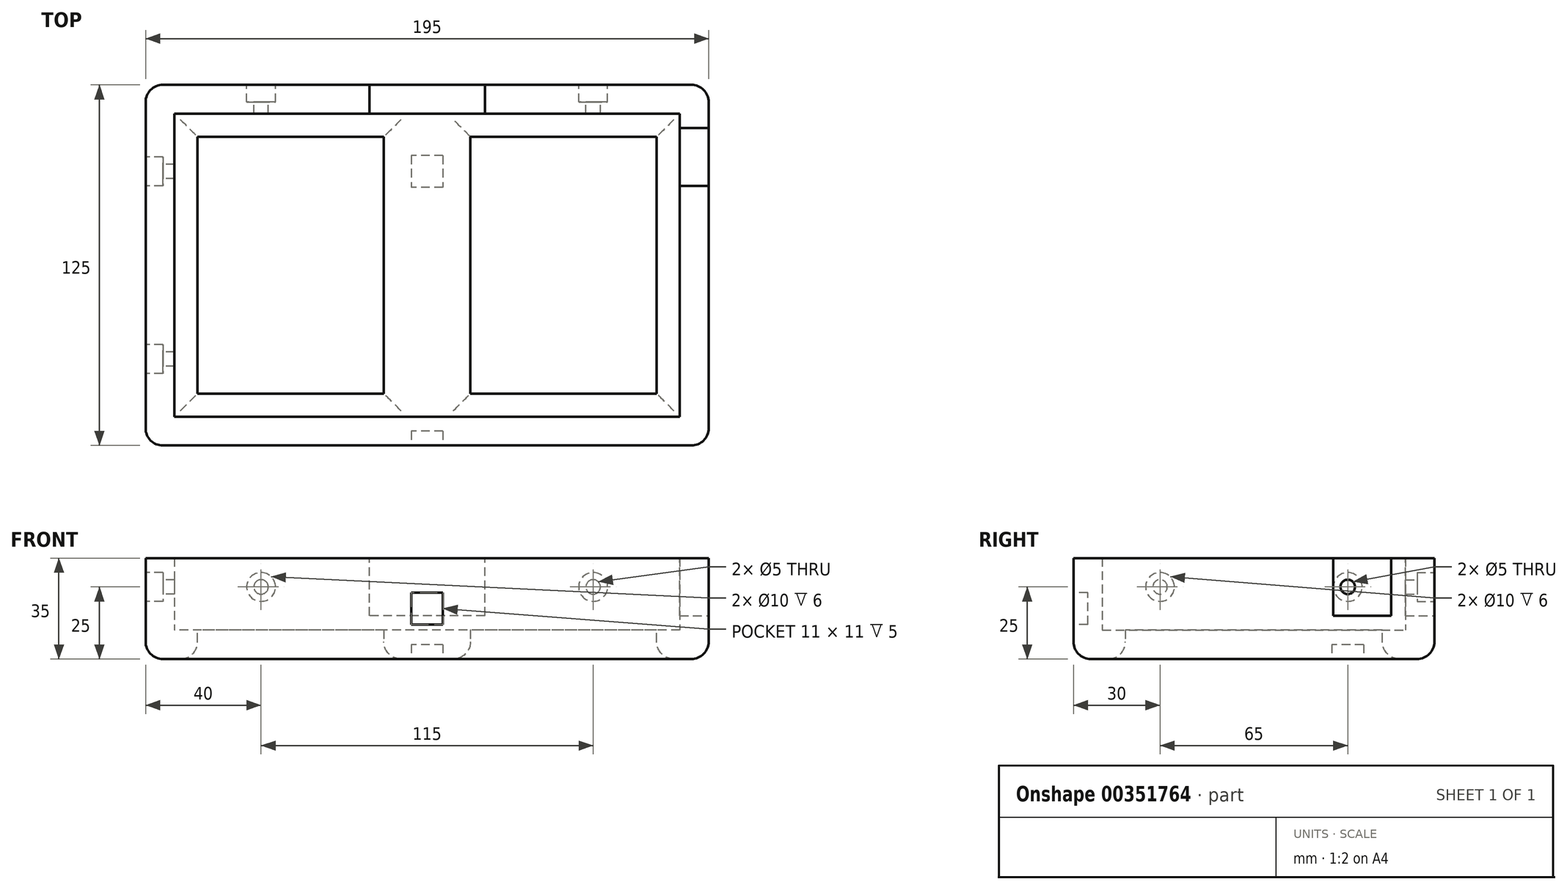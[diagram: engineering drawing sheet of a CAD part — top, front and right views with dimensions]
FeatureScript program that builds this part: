
annotation { "Feature Type Name" : "Feature", "Feature Type Description" : "" }
export const myFeature = defineFeature(function(context is Context, id is Id, definition is map)
    precondition{}
    {
        {
            var Q0;
            Q0=qCreatedBy(makeId("Top.planeOp"),FACE);
            var sketch = newSketch(context, id + "F0", { "sketchPlane" : qUnion([Q0])});
            skLineSegment(sketch, "E0.bottom", {"start": v(87.5, -52.5) * mm, "end": v(-87.5, -52.5) * mm});
            skLineSegment(sketch, "E0.top", {"start": v(87.5, 52.5) * mm, "end": v(-87.5, 52.5) * mm});
            skLineSegment(sketch, "E0.left", {"start": v(87.5, -52.5) * mm, "end": v(87.5, 52.5) * mm});
            skLineSegment(sketch, "E0.right", {"start": v(-87.5, -52.5) * mm, "end": v(-87.5, 52.5) * mm});
            skPoint(sketch, "E0.middle", {"position": v(0, 0) * mm});
            skLineSegment(sketch, "E1.0", {"start": v(97.5, -62.5) * mm, "end": v(97.5, 62.5) * mm});
            skLineSegment(sketch, "E1.1", {"start": v(97.5, -62.5) * mm, "end": v(-97.5, -62.5) * mm});
            skLineSegment(sketch, "E1.2", {"start": v(-97.5, -62.5) * mm, "end": v(-97.5, 62.5) * mm});
            skLineSegment(sketch, "E1.3", {"start": v(97.5, 62.5) * mm, "end": v(-97.5, 62.5) * mm});
            skSolve(sketch);
        }
        {
            var Q0;
            Q0=makeQuery(id+"F0.imprint","IMPRINT",FACE,{"disambiguationData":[TD([[makeQuery(id+"F0.imprint","IMPRINT",EDGE,{"derivedFrom":sQuery(id+"F0.wireOp",EDGE,"E0.bottom")}),1.0]])]});
            extrude(context, id + "F1", {"entities" : qUnion([Q0]), "depth" : 35 * mm});
        }
        {
            var Q0;
            Q0=makeQuery(id+"F0.imprint","IMPRINT",FACE,{"disambiguationData":[TD([[makeQuery(id+"F0.imprint","IMPRINT",EDGE,{"derivedFrom":sQuery(id+"F0.wireOp",EDGE,"E0.bottom")}),-1.0]])]});
            extrude(context, id + "F2", {"entities" : qUnion([Q0]), "operationType" : NewBodyOperationType.ADD, "depth" : 10 * mm});
        }
        {
            var Q0;
            Q0=makeQuery(id+"F1.opExtrude","CAP_FACE",FACE,{"disambiguationData":[OSD([sQuery(id+"F0.wireOp",EDGE,"E0.bottom"),sQuery(id+"F0.wireOp",EDGE,"E0.top"),sQuery(id+"F0.wireOp",EDGE,"E0.left"),sQuery(id+"F0.wireOp",EDGE,"E0.right"),sQuery(id+"F0.wireOp",EDGE,"E1.0"),sQuery(id+"F0.wireOp",EDGE,"E1.1"),sQuery(id+"F0.wireOp",EDGE,"E1.2"),sQuery(id+"F0.wireOp",EDGE,"E1.3")])],"isStart":false});
            var sketch = newSketch(context, id + "F3", { "sketchPlane" : qUnion([Q0])});
            skLineSegment(sketch, "E2.bottom", {"start": v(20, 52.5) * mm, "end": v(-20, 52.5) * mm});
            skLineSegment(sketch, "E2.top", {"start": v(20, 62.5) * mm, "end": v(-20, 62.5) * mm});
            skLineSegment(sketch, "E2.left", {"start": v(20, 52.5) * mm, "end": v(20, 62.5) * mm});
            skLineSegment(sketch, "E2.right", {"start": v(-20, 52.5) * mm, "end": v(-20, 62.5) * mm});
            skPoint(sketch, "E2.middle", {"position": v(0, 57.5) * mm});
            skLineSegment(sketch, "E3.bottom", {"start": v(87.5, 47.5) * mm, "end": v(97.5, 47.5) * mm});
            skLineSegment(sketch, "E3.top", {"start": v(87.5, 27.5) * mm, "end": v(97.5, 27.5) * mm});
            skLineSegment(sketch, "E3.left", {"start": v(87.5, 47.5) * mm, "end": v(87.5, 27.5) * mm});
            skLineSegment(sketch, "E3.right", {"start": v(97.5, 47.5) * mm, "end": v(97.5, 27.5) * mm});
            skSolve(sketch);
        }
        {
            var Q0;
            Q0=makeQuery(id+"F3.imprint","IMPRINT",FACE,{"disambiguationData":[TD([[makeQuery(id+"F3.imprint","IMPRINT",EDGE,{"derivedFrom":sQuery(id+"F3.wireOp",EDGE,"E2.bottom")}),-1.0]])]});
            var Q1;
            Q1=makeQuery(id+"F3.imprint","IMPRINT",FACE,{"disambiguationData":[TD([[makeQuery(id+"F3.imprint","IMPRINT",EDGE,{"derivedFrom":sQuery(id+"F3.wireOp",EDGE,"E3.bottom")}),-1.0]])]});
            extrude(context, id + "F4", {"entities" : qUnion([Q0, Q1]), "operationType" : NewBodyOperationType.REMOVE, "oppositeDirection" : true, "depth" : 20 * mm});
        }
        {
            var Q0;
            Q0=makeQuery(id+"F2.opExtrude","CAP_FACE",FACE,{"disambiguationData":[OSD([sQuery(id+"F0.wireOp",EDGE,"E0.bottom"),sQuery(id+"F0.wireOp",EDGE,"E0.top"),sQuery(id+"F0.wireOp",EDGE,"E0.left"),sQuery(id+"F0.wireOp",EDGE,"E0.right")])],"isStart":false});
            var sketch = newSketch(context, id + "F5", { "sketchPlane" : qUnion([Q0])});
            skLineSegment(sketch, "E4.bottom", {"start": v(79.5, -44.5) * mm, "end": v(-79.5, -44.5) * mm});
            skLineSegment(sketch, "E4.top", {"start": v(79.5, 44.5) * mm, "end": v(-79.5, 44.5) * mm});
            skLineSegment(sketch, "E4.left", {"start": v(79.5, -44.5) * mm, "end": v(79.5, 44.5) * mm});
            skLineSegment(sketch, "E4.right", {"start": v(-79.5, -44.5) * mm, "end": v(-79.5, 44.5) * mm});
            skPoint(sketch, "E4.middle", {"position": v(0, 0) * mm});
            skSolve(sketch);
        }
        {
            var Q0;
            Q0=makeQuery(id+"F5.imprint","IMPRINT",FACE,{"disambiguationData":[TD([[makeQuery(id+"F5.imprint","IMPRINT",EDGE,{"derivedFrom":sQuery(id+"F5.wireOp",EDGE,"E4.bottom")}),-1.0]])]});
            extrude(context, id + "F6", {"entities" : qUnion([Q0]), "operationType" : NewBodyOperationType.REMOVE, "oppositeDirection" : true, "depth" : 25 * mm});
        }
        {
            var Q0;
            Q0=makeQuery(id+"F1.opExtrude","SWEPT_FACE",FACE,{"disambiguationData":[OSD([sQuery(id+"F0.wireOp",EDGE,"E1.1")])]});
            var sketch = newSketch(context, id + "F7", { "sketchPlane" : qUnion([Q0])});
            skLineSegment(sketch, "E5.bottom", {"start": v(5.5, 12) * mm, "end": v(-5.5, 12) * mm});
            skLineSegment(sketch, "E5.top", {"start": v(5.5, 23) * mm, "end": v(-5.5, 23) * mm});
            skLineSegment(sketch, "E5.left", {"start": v(5.5, 12) * mm, "end": v(5.5, 23) * mm});
            skLineSegment(sketch, "E5.right", {"start": v(-5.5, 12) * mm, "end": v(-5.5, 23) * mm});
            skPoint(sketch, "E5.middle", {"position": v(0, 17.5) * mm});
            skSolve(sketch);
        }
        {
            var Q0;
            Q0=qCreatedBy(makeId("Top.planeOp"),FACE);
            var sketch = newSketch(context, id + "F8", { "sketchPlane" : qUnion([Q0])});
            skLineSegment(sketch, "E6.bottom", {"start": v(15, 55) * mm, "end": v(-15, 55) * mm});
            skLineSegment(sketch, "E6.top", {"start": v(15, -55) * mm, "end": v(-15, -55) * mm});
            skLineSegment(sketch, "E6.left", {"start": v(15, 55) * mm, "end": v(15, -55) * mm});
            skLineSegment(sketch, "E6.right", {"start": v(-15, 55) * mm, "end": v(-15, -55) * mm});
            skPoint(sketch, "E6.middle", {"position": v(0, 0) * mm});
            skSolve(sketch);
        }
        {
            var Q0;
            Q0=qSketchRegion(id+"F8",true);
            extrude(context, id + "F9", {"entities" : qUnion([Q0]), "operationType" : NewBodyOperationType.ADD, "depth" : 10 * mm});
        }
        {
            var Q0;
            Q0=qCreatedBy(makeId("Top.planeOp"),FACE);
            var sketch = newSketch(context, id + "F10", { "sketchPlane" : qUnion([Q0])});
            skLineSegment(sketch, "E7.bottom", {"start": v(5.5, 38) * mm, "end": v(-5.5, 38) * mm});
            skLineSegment(sketch, "E7.top", {"start": v(5.5, 27) * mm, "end": v(-5.5, 27) * mm});
            skLineSegment(sketch, "E7.left", {"start": v(5.5, 38) * mm, "end": v(5.5, 27) * mm});
            skLineSegment(sketch, "E7.right", {"start": v(-5.5, 38) * mm, "end": v(-5.5, 27) * mm});
            skPoint(sketch, "E7.middle", {"position": v(0, 32.5) * mm});
            skSolve(sketch);
        }
        {
            var Q0;
            Q0=makeQuery(id+"F10.imprint","IMPRINT",FACE,{"disambiguationData":[TD([[makeQuery(id+"F10.imprint","IMPRINT",EDGE,{"derivedFrom":sQuery(id+"F10.wireOp",EDGE,"E7.bottom")}),1.0]])]});
            extrude(context, id + "F11", {"entities" : qUnion([Q0]), "operationType" : NewBodyOperationType.REMOVE, "oppositeDirection" : true, "depth" : 5 * mm});
        }
        {
            var Q0;
            Q0=qSketchRegion(id+"F10",true);
            extrude(context, id + "F12", {"entities" : qUnion([Q0]), "operationType" : NewBodyOperationType.REMOVE, "depth" : 5 * mm});
        }
        {
            var Q0;
            Q0=makeQuery(id+"F1.opExtrude","SWEPT_FACE",FACE,{"disambiguationData":[OSD([sQuery(id+"F0.wireOp",EDGE,"E1.3")])]});
            var sketch = newSketch(context, id + "F13", { "sketchPlane" : qUnion([Q0])});
            skCircle(sketch, "E8", {"center": v(-57.5, 25) * mm, "radius": 2.5 * mm});
            skCircle(sketch, "E9", {"center": v(57.5, 25) * mm, "radius": 2.5 * mm});
            skSolve(sketch);
        }
        {
            var Q0;
            Q0=makeQuery(id+"F1.opExtrude","SWEPT_FACE",FACE,{"disambiguationData":[OSD([sQuery(id+"F0.wireOp",EDGE,"E1.2")])]});
            var sketch = newSketch(context, id + "F14", { "sketchPlane" : qUnion([Q0])});
            skCircle(sketch, "E10", {"center": v(-32.5, 25) * mm, "radius": 2.5 * mm});
            skCircle(sketch, "E11", {"center": v(32.5, 25) * mm, "radius": 2.5 * mm});
            skSolve(sketch);
        }
        {
            var Q0;
            Q0=sQuery(id+"F14.wireOp",VERTEX,"E10.center");
            var Q1;
            Q1=sQuery(id+"F14.wireOp",VERTEX,"E11.center");
            var Q2;
            Q2=makeQuery(id+"F1.opExtrude","SWEPT_BODY",BODY,{"disambiguationData":[OSD([sQuery(id+"F0.wireOp",EDGE,"E0.bottom"),sQuery(id+"F0.wireOp",EDGE,"E0.top"),sQuery(id+"F0.wireOp",EDGE,"E0.left"),sQuery(id+"F0.wireOp",EDGE,"E0.right"),sQuery(id+"F0.wireOp",EDGE,"E1.0"),sQuery(id+"F0.wireOp",EDGE,"E1.1"),sQuery(id+"F0.wireOp",EDGE,"E1.2"),sQuery(id+"F0.wireOp",EDGE,"E1.3")])]});
            hole(context, id + "F15", {"style" : HoleStyle.C_BORE, "endStyle" : HoleEndStyle.BLIND, "holeDiameter" : 5 * mm, "cBoreDiameter" : 10 * mm, "cBoreDepth" : 6 * mm, "holeDepth" : 12 * mm, "isTappedThrough" : true, "tappedDepth" : 12 * mm, "tapClearance" : 3, "locations" : qUnion([Q0, Q1]), "scope" : qUnion([Q2])});
        }
        {
            var Q0;
            Q0=sQuery(id+"F13.wireOp",VERTEX,"E8.center");
            var Q1;
            Q1=sQuery(id+"F13.wireOp",VERTEX,"E9.center");
            var Q2;
            Q2=makeQuery(id+"F1.opExtrude","SWEPT_BODY",BODY,{"disambiguationData":[OSD([sQuery(id+"F0.wireOp",EDGE,"E0.bottom"),sQuery(id+"F0.wireOp",EDGE,"E0.top"),sQuery(id+"F0.wireOp",EDGE,"E0.left"),sQuery(id+"F0.wireOp",EDGE,"E0.right"),sQuery(id+"F0.wireOp",EDGE,"E1.0"),sQuery(id+"F0.wireOp",EDGE,"E1.1"),sQuery(id+"F0.wireOp",EDGE,"E1.2"),sQuery(id+"F0.wireOp",EDGE,"E1.3")])]});
            hole(context, id + "F16", {"style" : HoleStyle.C_BORE, "endStyle" : HoleEndStyle.BLIND, "holeDiameter" : 5 * mm, "cBoreDiameter" : 10 * mm, "cBoreDepth" : 6 * mm, "holeDepth" : 12 * mm, "isTappedThrough" : true, "tappedDepth" : 12 * mm, "tapClearance" : 3, "locations" : qUnion([Q0, Q1]), "scope" : qUnion([Q2])});
        }
        {
            var Q0;
            {var subQ0=sQuery(id+"F0.wireOp",EDGE,"E0.right");var subQ1=sQuery(id+"F0.wireOp",EDGE,"E0.left");var subQ2=sQuery(id+"F0.wireOp",EDGE,"E0.top");var subQ3=sQuery(id+"F0.wireOp",EDGE,"E0.bottom");Q0=makeQuery(id+"F6.boolean.opBoolean","INTERSECT",EDGE,{"derivedFrom":[makeQuery(id+"F2.boolean.opBoolean","MERGE",FACE,{"derivedFrom":[makeQuery(id+"F1.opExtrude","CAP_FACE",FACE,{"disambiguationData":[OSD([subQ3,subQ2,subQ1,subQ0,sQuery(id+"F0.wireOp",EDGE,"E1.0"),sQuery(id+"F0.wireOp",EDGE,"E1.1"),sQuery(id+"F0.wireOp",EDGE,"E1.2"),sQuery(id+"F0.wireOp",EDGE,"E1.3")])],"isStart":true}),makeQuery(id+"F2.opExtrude","CAP_FACE",FACE,{"disambiguationData":[OSD([subQ3,subQ2,subQ1,subQ0])],"isStart":true})]}),makeQuery(id+"F6.opExtrude","SWEPT_FACE",FACE,{"disambiguationData":[OSD([sQuery(id+"F5.wireOp",EDGE,"E4.left")])]})]});}
            var Q1;
            {var subQ0=sQuery(id+"F0.wireOp",EDGE,"E0.right");var subQ1=sQuery(id+"F0.wireOp",EDGE,"E0.left");var subQ2=sQuery(id+"F0.wireOp",EDGE,"E0.top");var subQ3=sQuery(id+"F0.wireOp",EDGE,"E0.bottom");var subQ4=makeQuery(id+"F2.opExtrude","CAP_FACE",FACE,{"disambiguationData":[OSD([subQ3,subQ2,subQ1,subQ0])],"isStart":true});var subQ5=makeQuery(id+"F6.opExtrude","SWEPT_FACE",FACE,{"disambiguationData":[OSD([sQuery(id+"F5.wireOp",EDGE,"E4.top")])]});var subQ6=makeQuery(id+"F1.opExtrude","CAP_FACE",FACE,{"disambiguationData":[OSD([subQ3,subQ2,subQ1,subQ0,sQuery(id+"F0.wireOp",EDGE,"E1.0"),sQuery(id+"F0.wireOp",EDGE,"E1.1"),sQuery(id+"F0.wireOp",EDGE,"E1.2"),sQuery(id+"F0.wireOp",EDGE,"E1.3")])],"isStart":true});Q1=makeQuery(id+"F9.boolean.opBoolean","SPLIT",EDGE,{"disambiguationData":[TD([makeQuery(id+"F6.boolean.opBoolean","COPY",FACE,{"derivedFrom":makeQuery(id+"F6.opExtrude","SWEPT_FACE",FACE,{"disambiguationData":[OSD([sQuery(id+"F5.wireOp",EDGE,"E4.left")])]})})])],"derivedFrom":makeQuery(id+"F6.boolean.opBoolean","INTERSECT",EDGE,{"derivedFrom":[makeQuery(id+"F2.boolean.opBoolean","MERGE",FACE,{"derivedFrom":[subQ6,subQ4]}),subQ5]})});}
            var Q2;
            Q2=makeQuery(id+"F9.opExtrude","CAP_EDGE",EDGE,{"disambiguationData":[OSD([sQuery(id+"F8.wireOp",EDGE,"E6.left")])],"isStart":true});
            var Q3;
            {var subQ0=makeQuery(id+"F6.opExtrude","SWEPT_FACE",FACE,{"disambiguationData":[OSD([sQuery(id+"F5.wireOp",EDGE,"E4.bottom")])]});var subQ1=sQuery(id+"F0.wireOp",EDGE,"E0.right");var subQ2=sQuery(id+"F0.wireOp",EDGE,"E0.left");var subQ3=sQuery(id+"F0.wireOp",EDGE,"E0.top");var subQ4=sQuery(id+"F0.wireOp",EDGE,"E0.bottom");var subQ5=makeQuery(id+"F2.opExtrude","CAP_FACE",FACE,{"disambiguationData":[OSD([subQ4,subQ3,subQ2,subQ1])],"isStart":true});var subQ6=makeQuery(id+"F1.opExtrude","CAP_FACE",FACE,{"disambiguationData":[OSD([subQ4,subQ3,subQ2,subQ1,sQuery(id+"F0.wireOp",EDGE,"E1.0"),sQuery(id+"F0.wireOp",EDGE,"E1.1"),sQuery(id+"F0.wireOp",EDGE,"E1.2"),sQuery(id+"F0.wireOp",EDGE,"E1.3")])],"isStart":true});Q3=makeQuery(id+"F9.boolean.opBoolean","SPLIT",EDGE,{"disambiguationData":[TD([makeQuery(id+"F6.boolean.opBoolean","COPY",FACE,{"derivedFrom":makeQuery(id+"F6.opExtrude","SWEPT_FACE",FACE,{"disambiguationData":[OSD([sQuery(id+"F5.wireOp",EDGE,"E4.left")])]})})])],"derivedFrom":makeQuery(id+"F6.boolean.opBoolean","INTERSECT",EDGE,{"derivedFrom":[makeQuery(id+"F2.boolean.opBoolean","MERGE",FACE,{"derivedFrom":[subQ6,subQ5]}),subQ0]})});}
            var Q4;
            Q4=makeQuery(id+"F9.opExtrude","CAP_EDGE",EDGE,{"disambiguationData":[OSD([sQuery(id+"F8.wireOp",EDGE,"E6.right")])],"isStart":true});
            var Q5;
            {var subQ0=sQuery(id+"F0.wireOp",EDGE,"E0.right");var subQ1=sQuery(id+"F0.wireOp",EDGE,"E0.left");var subQ2=sQuery(id+"F0.wireOp",EDGE,"E0.top");var subQ3=sQuery(id+"F0.wireOp",EDGE,"E0.bottom");var subQ4=makeQuery(id+"F2.opExtrude","CAP_FACE",FACE,{"disambiguationData":[OSD([subQ3,subQ2,subQ1,subQ0])],"isStart":true});var subQ5=makeQuery(id+"F6.opExtrude","SWEPT_FACE",FACE,{"disambiguationData":[OSD([sQuery(id+"F5.wireOp",EDGE,"E4.top")])]});var subQ6=makeQuery(id+"F1.opExtrude","CAP_FACE",FACE,{"disambiguationData":[OSD([subQ3,subQ2,subQ1,subQ0,sQuery(id+"F0.wireOp",EDGE,"E1.0"),sQuery(id+"F0.wireOp",EDGE,"E1.1"),sQuery(id+"F0.wireOp",EDGE,"E1.2"),sQuery(id+"F0.wireOp",EDGE,"E1.3")])],"isStart":true});Q5=makeQuery(id+"F9.boolean.opBoolean","SPLIT",EDGE,{"disambiguationData":[TD([makeQuery(id+"F6.boolean.opBoolean","COPY",FACE,{"derivedFrom":makeQuery(id+"F6.opExtrude","SWEPT_FACE",FACE,{"disambiguationData":[OSD([sQuery(id+"F5.wireOp",EDGE,"E4.right")])]})})])],"derivedFrom":makeQuery(id+"F6.boolean.opBoolean","INTERSECT",EDGE,{"derivedFrom":[makeQuery(id+"F2.boolean.opBoolean","MERGE",FACE,{"derivedFrom":[subQ6,subQ4]}),subQ5]})});}
            var Q6;
            {var subQ0=sQuery(id+"F0.wireOp",EDGE,"E0.right");var subQ1=sQuery(id+"F0.wireOp",EDGE,"E0.left");var subQ2=sQuery(id+"F0.wireOp",EDGE,"E0.top");var subQ3=sQuery(id+"F0.wireOp",EDGE,"E0.bottom");Q6=makeQuery(id+"F6.boolean.opBoolean","INTERSECT",EDGE,{"derivedFrom":[makeQuery(id+"F2.boolean.opBoolean","MERGE",FACE,{"derivedFrom":[makeQuery(id+"F1.opExtrude","CAP_FACE",FACE,{"disambiguationData":[OSD([subQ3,subQ2,subQ1,subQ0,sQuery(id+"F0.wireOp",EDGE,"E1.0"),sQuery(id+"F0.wireOp",EDGE,"E1.1"),sQuery(id+"F0.wireOp",EDGE,"E1.2"),sQuery(id+"F0.wireOp",EDGE,"E1.3")])],"isStart":true}),makeQuery(id+"F2.opExtrude","CAP_FACE",FACE,{"disambiguationData":[OSD([subQ3,subQ2,subQ1,subQ0])],"isStart":true})]}),makeQuery(id+"F6.opExtrude","SWEPT_FACE",FACE,{"disambiguationData":[OSD([sQuery(id+"F5.wireOp",EDGE,"E4.right")])]})]});}
            var Q7;
            {var subQ0=makeQuery(id+"F6.opExtrude","SWEPT_FACE",FACE,{"disambiguationData":[OSD([sQuery(id+"F5.wireOp",EDGE,"E4.bottom")])]});var subQ1=sQuery(id+"F0.wireOp",EDGE,"E0.right");var subQ2=sQuery(id+"F0.wireOp",EDGE,"E0.left");var subQ3=sQuery(id+"F0.wireOp",EDGE,"E0.top");var subQ4=sQuery(id+"F0.wireOp",EDGE,"E0.bottom");var subQ5=makeQuery(id+"F2.opExtrude","CAP_FACE",FACE,{"disambiguationData":[OSD([subQ4,subQ3,subQ2,subQ1])],"isStart":true});var subQ6=makeQuery(id+"F1.opExtrude","CAP_FACE",FACE,{"disambiguationData":[OSD([subQ4,subQ3,subQ2,subQ1,sQuery(id+"F0.wireOp",EDGE,"E1.0"),sQuery(id+"F0.wireOp",EDGE,"E1.1"),sQuery(id+"F0.wireOp",EDGE,"E1.2"),sQuery(id+"F0.wireOp",EDGE,"E1.3")])],"isStart":true});Q7=makeQuery(id+"F9.boolean.opBoolean","SPLIT",EDGE,{"disambiguationData":[TD([makeQuery(id+"F6.boolean.opBoolean","COPY",FACE,{"derivedFrom":makeQuery(id+"F6.opExtrude","SWEPT_FACE",FACE,{"disambiguationData":[OSD([sQuery(id+"F5.wireOp",EDGE,"E4.right")])]})})])],"derivedFrom":makeQuery(id+"F6.boolean.opBoolean","INTERSECT",EDGE,{"derivedFrom":[makeQuery(id+"F2.boolean.opBoolean","MERGE",FACE,{"derivedFrom":[subQ6,subQ5]}),subQ0]})});}
            fillet(context, id + "F17", {"entities" : qUnion([Q0, Q1, Q2, Q3, Q4, Q5, Q6, Q7]), "radius" : 6 * mm, "tangentPropagation" : true, "allowEdgeOverflow" : false});
        }
        {
            var Q0;
            Q0=makeQuery(id+"F1.opExtrude","CAP_EDGE",EDGE,{"disambiguationData":[OSD([sQuery(id+"F0.wireOp",EDGE,"E1.3")])],"isStart":true});
            var Q1;
            Q1=makeQuery(id+"F1.opExtrude","CAP_EDGE",EDGE,{"disambiguationData":[OSD([sQuery(id+"F0.wireOp",EDGE,"E1.0")])],"isStart":true});
            var Q2;
            Q2=makeQuery(id+"F1.opExtrude","CAP_EDGE",EDGE,{"disambiguationData":[OSD([sQuery(id+"F0.wireOp",EDGE,"E1.1")])],"isStart":true});
            var Q3;
            Q3=makeQuery(id+"F1.opExtrude","CAP_EDGE",EDGE,{"disambiguationData":[OSD([sQuery(id+"F0.wireOp",EDGE,"E1.2")])],"isStart":true});
            var Q4;
            Q4=makeQuery(id+"F1.opExtrude","SWEPT_EDGE",EDGE,{"disambiguationData":[OSD([sQuery(id+"F0.wireOp",EDGE,"E1.2"),sQuery(id+"F0.wireOp",EDGE,"E1.3")])]});
            var Q5;
            Q5=makeQuery(id+"F1.opExtrude","SWEPT_EDGE",EDGE,{"disambiguationData":[OSD([sQuery(id+"F0.wireOp",EDGE,"E1.0"),sQuery(id+"F0.wireOp",EDGE,"E1.3")])]});
            var Q6;
            Q6=makeQuery(id+"F1.opExtrude","SWEPT_EDGE",EDGE,{"disambiguationData":[OSD([sQuery(id+"F0.wireOp",EDGE,"E1.0"),sQuery(id+"F0.wireOp",EDGE,"E1.1")])]});
            var Q7;
            Q7=makeQuery(id+"F1.opExtrude","SWEPT_EDGE",EDGE,{"disambiguationData":[OSD([sQuery(id+"F0.wireOp",EDGE,"E1.1"),sQuery(id+"F0.wireOp",EDGE,"E1.2")])]});
            fillet(context, id + "F18", {"entities" : qUnion([Q0, Q1, Q2, Q3, Q4, Q5, Q6, Q7]), "radius" : 6 * mm, "tangentPropagation" : true, "allowEdgeOverflow" : false});
        }
        {
            var Q0;
            Q0=makeQuery(id+"F7.imprint","IMPRINT",FACE,{"disambiguationData":[TD([[makeQuery(id+"F7.imprint","IMPRINT",EDGE,{"derivedFrom":sQuery(id+"F7.wireOp",EDGE,"E5.bottom")}),-1.0]])]});
            var Q1;
            Q1=sQuery(id+"F7.wireOp",EDGE,"E5.top");
            var Q2;
            Q2=sQuery(id+"F7.wireOp",EDGE,"E5.right");
            var Q3;
            Q3=sQuery(id+"F7.wireOp",EDGE,"E5.bottom");
            var Q4;
            Q4=sQuery(id+"F7.wireOp",EDGE,"E5.left");
            extrude(context, id + "F19", {"entities" : qUnion([Q0]), "operationType" : NewBodyOperationType.REMOVE, "surfaceEntities" : qUnion([Q1, Q2, Q3, Q4]), "oppositeDirection" : true, "depth" : 5 * mm});
        }
    });
